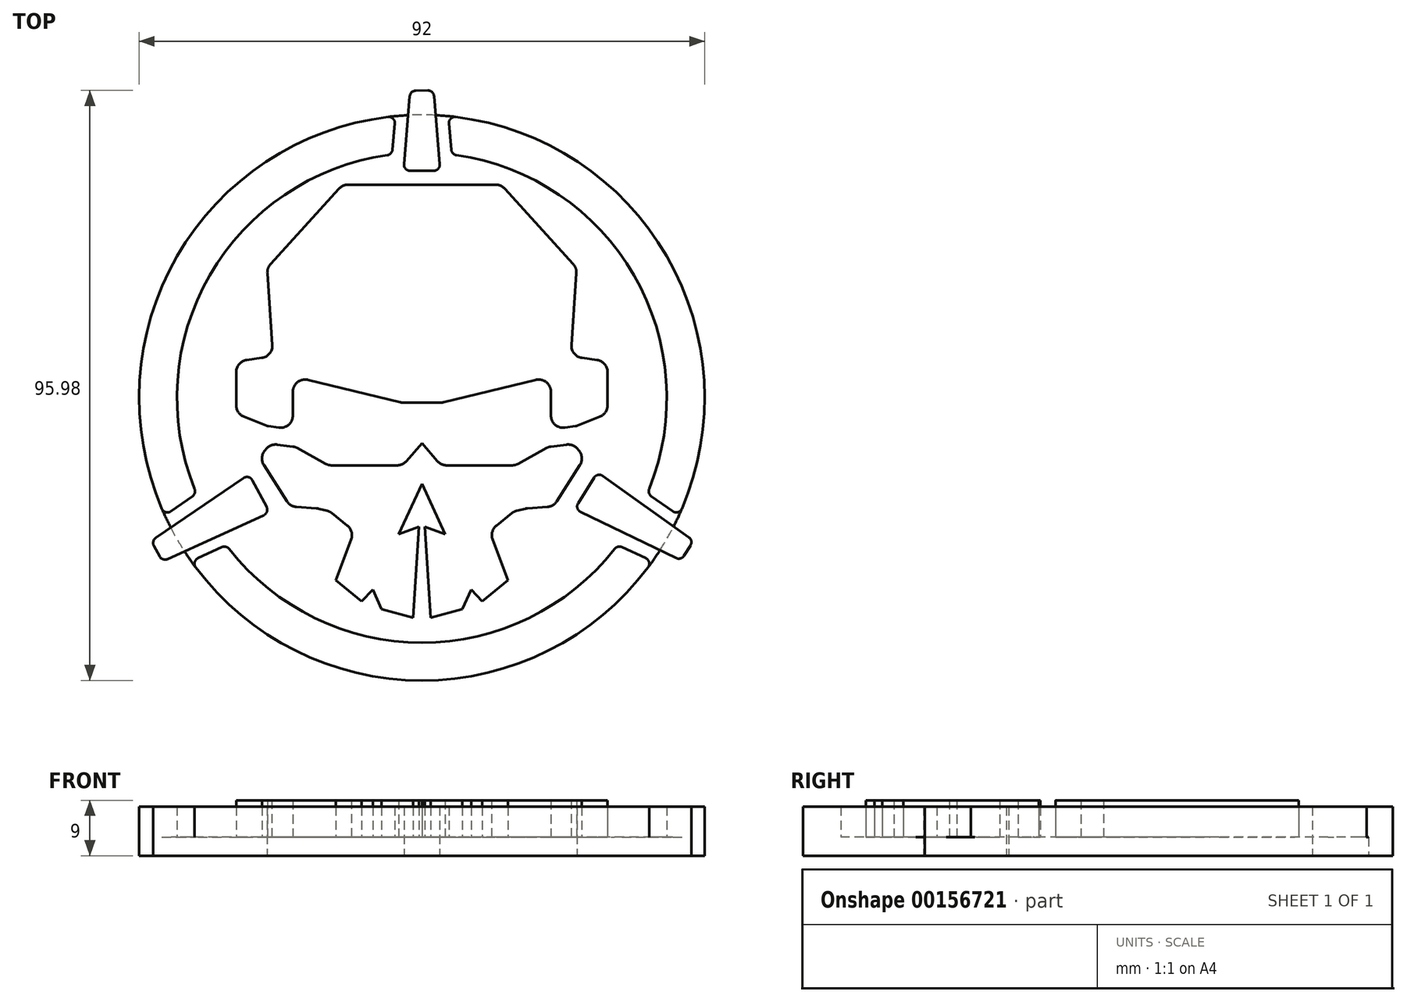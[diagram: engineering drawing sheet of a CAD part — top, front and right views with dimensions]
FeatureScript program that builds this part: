
annotation { "Feature Type Name" : "Feature", "Feature Type Description" : "" }
export const myFeature = defineFeature(function(context is Context, id is Id, definition is map)
    precondition{}
    {
        {
            var Q0;
            Q0=qCreatedBy(makeId("Top.planeOp"),FACE);
            cPlane(context, id + "F0", {"entities" : qUnion([Q0]), "cplaneType" : CPlaneType.OFFSET, "offset" : 3 * mm, "oppositeDirection" : true, "width" : 150 * mm, "height" : 150 * mm});
        }
        {
            var Q0;
            Q0=qCreatedBy(id+"F0.planeOp",FACE);
            var sketch = newSketch(context, id + "F1", { "sketchPlane" : qUnion([Q0])});
            skCircle(sketch, "E0", {"center": v(0, 0) * mm, "radius": 46 * mm});
            skSolve(sketch);
        }
        {
            var Q0;
            Q0 = qSketchRegion(id + "F1", true);
            extrude(context, id + "F2", {"entities" : qUnion([Q0]), "depth" : 8 * mm});
        }
        {
            var Q0;
            Q0=qCreatedBy(makeId("Top.planeOp"),FACE);
            var sketch = newSketch(context, id + "F3", { "sketchPlane" : qUnion([Q0])});
            skCircle(sketch, "E1", {"center": v(0, 0) * mm, "radius": 39.85 * mm});
            skSolve(sketch);
        }
        {
            var Q0;
            Q0 = qSketchRegion(id + "F3", true);
            extrude(context, id + "F4", {"entities" : qUnion([Q0]), "depth" : 6 * mm});
        }
        {
            var Q0;
            Q0=makeQuery(id+"F4.opExtrude","SWEPT_BODY",BODY,{"disambiguationData":[OSD([sQuery(id+"F3.wireOp",EDGE,"E1")])]});
            var Q1;
            Q1=makeQuery(id+"F2.opExtrude","SWEPT_BODY",BODY,{"disambiguationData":[OSD([sQuery(id+"F1.wireOp",EDGE,"E0")])]});
            booleanBodies(context, id + "F5", {"operationType" : BooleanOperationType.SUBTRACTION, "tools" : qUnion([Q0]), "targets" : qUnion([Q1])});
        }
        {
            var Q0;
            Q0=qCreatedBy(makeId("Top.planeOp"),FACE);
            var sketch = newSketch(context, id + "F6", { "sketchPlane" : qUnion([Q0])});
            skLineSegment(sketch, "E2", {"start": v(-4.2, 46.75) * mm, "end": v(-5, 38) * mm});
            skLineSegment(sketch, "E3", {"start": v(-5, 38) * mm, "end": v(5, 38) * mm});
            skLineSegment(sketch, "E4", {"start": v(5, 38) * mm, "end": v(4.2, 46.75) * mm});
            skLineSegment(sketch, "E5", {"start": v(4.2, 46.75) * mm, "end": v(-4.2, 46.75) * mm});
            skSolve(sketch);
        }
        {
            var Q0;
            Q0 = qSketchRegion(id + "F6", true);
            extrude(context, id + "F7", {"entities" : qUnion([Q0]), "depth" : 25 * mm});
        }
        {
            var Q0;
            Q0=qCreatedBy(makeId("Right.planeOp"),FACE);
            var sketch = newSketch(context, id + "F8", { "sketchPlane" : qUnion([Q0])});
            skLineSegment(sketch, "E6", {"start": v(0, 40.83) * mm, "end": v(0, -33.75) * mm});
            skSolve(sketch);
        }
        {
            var Q0;
            Q0=makeQuery(id+"F7.opExtrude","SWEPT_BODY",BODY,{"disambiguationData":[OSD([sQuery(id+"F6.wireOp",EDGE,"E2"),sQuery(id+"F6.wireOp",EDGE,"E3"),sQuery(id+"F6.wireOp",EDGE,"E4"),sQuery(id+"F6.wireOp",EDGE,"E5")])]});
            var Q1;
            Q1=qCreatedBy(makeId("Origin.pointOp"),VERTEX);
            var Q2;
            Q2=sQuery(id+"F8.wireOp",EDGE,"E6");
            transform(context, id + "F9", {"entities" : qUnion([Q0]), "transformType" : TransformType.ROTATION, "transformAxis" : qUnion([Q2]), "angle" : 120 * degree, "makeCopy" : true});
        }
        {
            var Q0;
            Q0=makeQuery(id+"F9.opPattern","COPY",BODY,{"derivedFrom":makeQuery(id+"F7.opExtrude","SWEPT_BODY",BODY,{"disambiguationData":[OSD([sQuery(id+"F6.wireOp",EDGE,"E2"),sQuery(id+"F6.wireOp",EDGE,"E3"),sQuery(id+"F6.wireOp",EDGE,"E4"),sQuery(id+"F6.wireOp",EDGE,"E5")])]}),"instanceName":"1"});
            var Q1;
            Q1=sQuery(id+"F8.wireOp",EDGE,"E6");
            transform(context, id + "F10", {"entities" : qUnion([Q0]), "transformType" : TransformType.ROTATION, "transformAxis" : qUnion([Q1]), "angle" : 120 * degree, "makeCopy" : true});
        }
        {
            var Q0;
            Q0=makeQuery(id+"F10.opPattern","COPY",BODY,{"derivedFrom":makeQuery(id+"F9.opPattern","COPY",BODY,{"derivedFrom":makeQuery(id+"F7.opExtrude","SWEPT_BODY",BODY,{"disambiguationData":[OSD([sQuery(id+"F6.wireOp",EDGE,"E2"),sQuery(id+"F6.wireOp",EDGE,"E3"),sQuery(id+"F6.wireOp",EDGE,"E4"),sQuery(id+"F6.wireOp",EDGE,"E5")])]}),"instanceName":"1"}),"instanceName":"1"});
            var Q1;
            Q1=makeQuery(id+"F9.opPattern","COPY",BODY,{"derivedFrom":makeQuery(id+"F7.opExtrude","SWEPT_BODY",BODY,{"disambiguationData":[OSD([sQuery(id+"F6.wireOp",EDGE,"E2"),sQuery(id+"F6.wireOp",EDGE,"E3"),sQuery(id+"F6.wireOp",EDGE,"E4"),sQuery(id+"F6.wireOp",EDGE,"E5")])]}),"instanceName":"1"});
            var Q2;
            Q2=makeQuery(id+"F7.opExtrude","SWEPT_BODY",BODY,{"disambiguationData":[OSD([sQuery(id+"F6.wireOp",EDGE,"E2"),sQuery(id+"F6.wireOp",EDGE,"E3"),sQuery(id+"F6.wireOp",EDGE,"E4"),sQuery(id+"F6.wireOp",EDGE,"E5")])]});
            var Q3;
            Q3=makeQuery(id+"F2.opExtrude","SWEPT_BODY",BODY,{"disambiguationData":[OSD([sQuery(id+"F1.wireOp",EDGE,"E0")])]});
            booleanBodies(context, id + "F11", {"operationType" : BooleanOperationType.SUBTRACTION, "tools" : qUnion([Q0, Q1, Q2]), "targets" : qUnion([Q3])});
        }
        {
            var Q0;
            Q0=qCreatedBy(id+"F0.planeOp",FACE);
            var sketch = newSketch(context, id + "F12", { "sketchPlane" : qUnion([Q0])});
            skLineSegment(sketch, "E7", {"start": v(-1.9, 49.93) * mm, "end": v(-3, 36.9) * mm});
            skLineSegment(sketch, "E8", {"start": v(-3, 36.9) * mm, "end": v(3, 36.9) * mm});
            skLineSegment(sketch, "E9", {"start": v(3, 36.9) * mm, "end": v(1.9, 50) * mm});
            skLineSegment(sketch, "E10", {"start": v(1.9, 50) * mm, "end": v(-1.9, 49.93) * mm});
            skSolve(sketch);
        }
        {
            var Q0;
            Q0 = qSketchRegion(id + "F12", true);
            extrude(context, id + "F13", {"entities" : qUnion([Q0]), "depth" : 8 * mm});
        }
        {
            var Q0;
            Q0=qCreatedBy(id+"F0.planeOp",FACE);
            var sketch = newSketch(context, id + "F14", { "sketchPlane" : qUnion([Q0])});
            skLineSegment(sketch, "E11", {"start": v(44.18, -23.23) * mm, "end": v(28.57, -12.11) * mm});
            skLineSegment(sketch, "E12", {"start": v(28.57, -12.11) * mm, "end": v(24.82, -18.1) * mm});
            skLineSegment(sketch, "E13", {"start": v(24.82, -18.1) * mm, "end": v(42.18, -26.48) * mm});
            skLineSegment(sketch, "E14", {"start": v(42.18, -26.48) * mm, "end": v(44.18, -23.23) * mm});
            skSolve(sketch);
        }
        {
            var Q0;
            Q0 = qSketchRegion(id + "F14", true);
            extrude(context, id + "F15", {"entities" : qUnion([Q0]), "depth" : 8 * mm});
        }
        {
            var Q0;
            Q0=makeQuery(id+"F15.opExtrude","SWEPT_BODY",BODY,{"disambiguationData":[OSD([sQuery(id+"F14.wireOp",EDGE,"E11"),sQuery(id+"F14.wireOp",EDGE,"E12"),sQuery(id+"F14.wireOp",EDGE,"E13"),sQuery(id+"F14.wireOp",EDGE,"E14")])]});
            var Q1;
            Q1=sQuery(id+"F8.wireOp",EDGE,"E6");
            transform(context, id + "F16", {"entities" : qUnion([Q0]), "transformType" : TransformType.ROTATION, "transformAxis" : qUnion([Q1]), "angle" : 120 * degree, "makeCopy" : true});
        }
        {
            var Q0;
            Q0=qCreatedBy(makeId("Top.planeOp"),FACE);
            var sketch = newSketch(context, id + "F17", { "sketchPlane" : qUnion([Q0])});
            skLineSegment(sketch, "E15", {"start": v(12.9, 34.65) * mm, "end": v(-12.9, 34.65) * mm});
            skLineSegment(sketch, "E16", {"start": v(-12.9, 34.65) * mm, "end": v(-25.2, 21.1) * mm});
            skLineSegment(sketch, "E17", {"start": v(-25.2, 21.1) * mm, "end": v(-24.2, 6.73) * mm});
            skLineSegment(sketch, "E18", {"start": v(-24.2, 6.73) * mm, "end": v(-30.2, 5.9) * mm});
            skLineSegment(sketch, "E19", {"start": v(-30.2, 5.9) * mm, "end": v(-30.2, -2.6) * mm});
            skLineSegment(sketch, "E20", {"start": v(-30.2, -2.6) * mm, "end": v(-25.2, -4.6) * mm});
            skLineSegment(sketch, "E21", {"start": v(-25.2, -4.6) * mm, "end": v(-21, -5.2) * mm});
            skLineSegment(sketch, "E22", {"start": v(-21, -5.2) * mm, "end": v(-21, 3.5) * mm});
            skLineSegment(sketch, "E23", {"start": v(-21, 3.5) * mm, "end": v(-3.3, -0.8) * mm});
            skLineSegment(sketch, "E24", {"start": v(-3.3, -0.8) * mm, "end": v(3.3, -0.8) * mm});
            skLineSegment(sketch, "E25", {"start": v(3.3, -0.8) * mm, "end": v(21, 3.5) * mm});
            skLineSegment(sketch, "E26", {"start": v(21, 3.5) * mm, "end": v(21, -5.2) * mm});
            skLineSegment(sketch, "E27", {"start": v(21, -5.2) * mm, "end": v(25.2, -4.6) * mm});
            skLineSegment(sketch, "E28", {"start": v(25.2, -4.6) * mm, "end": v(30.2, -2.6) * mm});
            skLineSegment(sketch, "E29", {"start": v(30.2, -2.6) * mm, "end": v(30.2, 5.9) * mm});
            skLineSegment(sketch, "E30", {"start": v(30.2, 5.9) * mm, "end": v(24.2, 6.73) * mm});
            skLineSegment(sketch, "E31", {"start": v(24.2, 6.73) * mm, "end": v(25.2, 21.1) * mm});
            skLineSegment(sketch, "E32", {"start": v(25.2, 21.1) * mm, "end": v(12.9, 34.65) * mm});
            skSolve(sketch);
        }
        {
            var Q0;
            Q0 = qSketchRegion(id + "F17", true);
            extrude(context, id + "F18", {"entities" : qUnion([Q0]), "depth" : 6 * mm});
        }
        {
            var Q0;
            Q0=qCreatedBy(makeId("Top.planeOp"),FACE);
            var sketch = newSketch(context, id + "F19", { "sketchPlane" : qUnion([Q0])});
            skLineSegment(sketch, "E33", {"start": v(0, -7.4) * mm, "end": v(-3.1, -11) * mm});
            skLineSegment(sketch, "E34", {"start": v(-3.1, -11) * mm, "end": v(-15.2, -11) * mm});
            skLineSegment(sketch, "E35", {"start": v(-15.2, -11) * mm, "end": v(-20.6, -8) * mm});
            skLineSegment(sketch, "E36", {"start": v(-20.6, -8) * mm, "end": v(-24.6, -7.5) * mm});
            skLineSegment(sketch, "E37", {"start": v(-24.6, -7.5) * mm, "end": v(-26.5, -9.7) * mm});
            skLineSegment(sketch, "E38", {"start": v(-26.5, -9.7) * mm, "end": v(-21.4, -17.7) * mm});
            skLineSegment(sketch, "E39", {"start": v(-21.4, -17.7) * mm, "end": v(-17, -18) * mm});
            skLineSegment(sketch, "E40", {"start": v(-17, -18) * mm, "end": v(-15, -18.5) * mm});
            skLineSegment(sketch, "E41", {"start": v(-15, -18.5) * mm, "end": v(-11, -21.7) * mm});
            skLineSegment(sketch, "E42", {"start": v(-11, -21.7) * mm, "end": v(-14, -29.7) * mm});
            skLineSegment(sketch, "E43", {"start": v(-14, -29.7) * mm, "end": v(-9.8, -33.1) * mm});
            skLineSegment(sketch, "E44", {"start": v(-9.8, -33.1) * mm, "end": v(-8, -31.2) * mm});
            skLineSegment(sketch, "E45", {"start": v(-8, -31.2) * mm, "end": v(-6.6, -34.4) * mm});
            skLineSegment(sketch, "E46", {"start": v(-6.6, -34.4) * mm, "end": v(-1.4, -35.8) * mm});
            skLineSegment(sketch, "E47", {"start": v(-1.4, -35.8) * mm, "end": v(-0.5, -21) * mm});
            skLineSegment(sketch, "E48", {"start": v(-0.5, -21) * mm, "end": v(-3.8, -22.2) * mm});
            skLineSegment(sketch, "E49", {"start": v(-3.8, -22.2) * mm, "end": v(0, -14) * mm});
            skLineSegment(sketch, "E50", {"start": v(0, -14) * mm, "end": v(3.8, -22.2) * mm});
            skLineSegment(sketch, "E51", {"start": v(3.8, -22.2) * mm, "end": v(0.5, -21) * mm});
            skLineSegment(sketch, "E52", {"start": v(0.5, -21) * mm, "end": v(1.4, -35.8) * mm});
            skLineSegment(sketch, "E53", {"start": v(1.4, -35.8) * mm, "end": v(6.6, -34.4) * mm});
            skLineSegment(sketch, "E54", {"start": v(6.6, -34.4) * mm, "end": v(8, -31.2) * mm});
            skLineSegment(sketch, "E55", {"start": v(8, -31.2) * mm, "end": v(9.8, -33.1) * mm});
            skLineSegment(sketch, "E56", {"start": v(9.8, -33.1) * mm, "end": v(14, -29.7) * mm});
            skLineSegment(sketch, "E57", {"start": v(14, -29.7) * mm, "end": v(11, -21.7) * mm});
            skLineSegment(sketch, "E58", {"start": v(11, -21.7) * mm, "end": v(15, -18.5) * mm});
            skLineSegment(sketch, "E59", {"start": v(15, -18.5) * mm, "end": v(17, -18) * mm});
            skLineSegment(sketch, "E60", {"start": v(17, -18) * mm, "end": v(21.4, -17.7) * mm});
            skLineSegment(sketch, "E61", {"start": v(21.4, -17.7) * mm, "end": v(26.5, -9.7) * mm});
            skLineSegment(sketch, "E62", {"start": v(26.5, -9.7) * mm, "end": v(24.6, -7.5) * mm});
            skLineSegment(sketch, "E63", {"start": v(24.6, -7.5) * mm, "end": v(20.6, -8) * mm});
            skLineSegment(sketch, "E64", {"start": v(20.6, -8) * mm, "end": v(15.2, -11) * mm});
            skLineSegment(sketch, "E65", {"start": v(15.2, -11) * mm, "end": v(3.1, -11) * mm});
            skLineSegment(sketch, "E66", {"start": v(3.1, -11) * mm, "end": v(0, -7.4) * mm});
            skSolve(sketch);
        }
        {
            var Q0;
            Q0 = qSketchRegion(id + "F19", true);
            extrude(context, id + "F20", {"entities" : qUnion([Q0]), "depth" : 6 * mm});
        }
        {
            var Q0;
            Q0=makeQuery(id+"F13.opExtrude","SWEPT_EDGE",EDGE,{"disambiguationData":[OSD([sQuery(id+"F12.wireOp",EDGE,"E9"),sQuery(id+"F12.wireOp",EDGE,"E10")])]});
            var Q1;
            Q1=makeQuery(id+"F13.opExtrude","SWEPT_EDGE",EDGE,{"disambiguationData":[OSD([sQuery(id+"F12.wireOp",EDGE,"E7"),sQuery(id+"F12.wireOp",EDGE,"E10")])]});
            var Q2;
            Q2=makeQuery(id+"F13.opExtrude","SWEPT_EDGE",EDGE,{"disambiguationData":[OSD([sQuery(id+"F12.wireOp",EDGE,"E8"),sQuery(id+"F12.wireOp",EDGE,"E9")])]});
            var Q3;
            Q3=makeQuery(id+"F13.opExtrude","SWEPT_EDGE",EDGE,{"disambiguationData":[OSD([sQuery(id+"F12.wireOp",EDGE,"E7"),sQuery(id+"F12.wireOp",EDGE,"E8")])]});
            var Q4;
            Q4=makeQuery(id+"F16.opPattern","COPY",EDGE,{"derivedFrom":makeQuery(id+"F15.opExtrude","SWEPT_EDGE",EDGE,{"disambiguationData":[OSD([sQuery(id+"F14.wireOp",EDGE,"E12"),sQuery(id+"F14.wireOp",EDGE,"E13")])]}),"instanceName":"1"});
            var Q5;
            Q5=makeQuery(id+"F16.opPattern","COPY",EDGE,{"derivedFrom":makeQuery(id+"F15.opExtrude","SWEPT_EDGE",EDGE,{"disambiguationData":[OSD([sQuery(id+"F14.wireOp",EDGE,"E13"),sQuery(id+"F14.wireOp",EDGE,"E14")])]}),"instanceName":"1"});
            var Q6;
            Q6=makeQuery(id+"F16.opPattern","COPY",EDGE,{"derivedFrom":makeQuery(id+"F15.opExtrude","SWEPT_EDGE",EDGE,{"disambiguationData":[OSD([sQuery(id+"F14.wireOp",EDGE,"E11"),sQuery(id+"F14.wireOp",EDGE,"E14")])]}),"instanceName":"1"});
            var Q7;
            Q7=makeQuery(id+"F16.opPattern","COPY",EDGE,{"derivedFrom":makeQuery(id+"F15.opExtrude","SWEPT_EDGE",EDGE,{"disambiguationData":[OSD([sQuery(id+"F14.wireOp",EDGE,"E11"),sQuery(id+"F14.wireOp",EDGE,"E12")])]}),"instanceName":"1"});
            var Q8;
            Q8=makeQuery(id+"F15.opExtrude","SWEPT_EDGE",EDGE,{"disambiguationData":[OSD([sQuery(id+"F14.wireOp",EDGE,"E12"),sQuery(id+"F14.wireOp",EDGE,"E13")])]});
            var Q9;
            Q9=makeQuery(id+"F15.opExtrude","SWEPT_EDGE",EDGE,{"disambiguationData":[OSD([sQuery(id+"F14.wireOp",EDGE,"E11"),sQuery(id+"F14.wireOp",EDGE,"E12")])]});
            var Q10;
            Q10=makeQuery(id+"F15.opExtrude","SWEPT_EDGE",EDGE,{"disambiguationData":[OSD([sQuery(id+"F14.wireOp",EDGE,"E13"),sQuery(id+"F14.wireOp",EDGE,"E14")])]});
            var Q11;
            Q11=makeQuery(id+"F15.opExtrude","SWEPT_EDGE",EDGE,{"disambiguationData":[OSD([sQuery(id+"F14.wireOp",EDGE,"E11"),sQuery(id+"F14.wireOp",EDGE,"E14")])]});
            var Q12;
            Q12=makeQuery(id+"F11.opBoolean","INTERSECT",EDGE,{"derivedFrom":[makeQuery(id+"F2.opExtrude","SWEPT_FACE",FACE,{"disambiguationData":[OSD([sQuery(id+"F1.wireOp",EDGE,"E0")])]}),makeQuery(id+"F9.opPattern","COPY",FACE,{"derivedFrom":makeQuery(id+"F7.opExtrude","SWEPT_FACE",FACE,{"disambiguationData":[OSD([sQuery(id+"F6.wireOp",EDGE,"E4")])]}),"instanceName":"1"})]});
            var Q13;
            Q13=makeQuery(id+"F11.opBoolean","INTERSECT",EDGE,{"derivedFrom":[makeQuery(id+"F2.opExtrude","SWEPT_FACE",FACE,{"disambiguationData":[OSD([sQuery(id+"F1.wireOp",EDGE,"E0")])]}),makeQuery(id+"F9.opPattern","COPY",FACE,{"derivedFrom":makeQuery(id+"F7.opExtrude","SWEPT_FACE",FACE,{"disambiguationData":[OSD([sQuery(id+"F6.wireOp",EDGE,"E2")])]}),"instanceName":"1"})]});
            var Q14;
            Q14=makeQuery(id+"F11.opBoolean","INTERSECT",EDGE,{"derivedFrom":[makeQuery(id+"F5.opBoolean","COPY",FACE,{"derivedFrom":makeQuery(id+"F4.opExtrude","SWEPT_FACE",FACE,{"disambiguationData":[OSD([sQuery(id+"F3.wireOp",EDGE,"E1")])]})}),makeQuery(id+"F9.opPattern","COPY",FACE,{"derivedFrom":makeQuery(id+"F7.opExtrude","SWEPT_FACE",FACE,{"disambiguationData":[OSD([sQuery(id+"F6.wireOp",EDGE,"E2")])]}),"instanceName":"1"})]});
            var Q15;
            Q15=makeQuery(id+"F11.opBoolean","INTERSECT",EDGE,{"derivedFrom":[makeQuery(id+"F5.opBoolean","COPY",FACE,{"derivedFrom":makeQuery(id+"F4.opExtrude","SWEPT_FACE",FACE,{"disambiguationData":[OSD([sQuery(id+"F3.wireOp",EDGE,"E1")])]})}),makeQuery(id+"F9.opPattern","COPY",FACE,{"derivedFrom":makeQuery(id+"F7.opExtrude","SWEPT_FACE",FACE,{"disambiguationData":[OSD([sQuery(id+"F6.wireOp",EDGE,"E4")])]}),"instanceName":"1"})]});
            var Q16;
            Q16=makeQuery(id+"F11.opBoolean","INTERSECT",EDGE,{"derivedFrom":[makeQuery(id+"F2.opExtrude","SWEPT_FACE",FACE,{"disambiguationData":[OSD([sQuery(id+"F1.wireOp",EDGE,"E0")])]}),makeQuery(id+"F7.opExtrude","SWEPT_FACE",FACE,{"disambiguationData":[OSD([sQuery(id+"F6.wireOp",EDGE,"E4")])]})]});
            var Q17;
            Q17=makeQuery(id+"F11.opBoolean","INTERSECT",EDGE,{"derivedFrom":[makeQuery(id+"F2.opExtrude","SWEPT_FACE",FACE,{"disambiguationData":[OSD([sQuery(id+"F1.wireOp",EDGE,"E0")])]}),makeQuery(id+"F7.opExtrude","SWEPT_FACE",FACE,{"disambiguationData":[OSD([sQuery(id+"F6.wireOp",EDGE,"E2")])]})]});
            var Q18;
            Q18=makeQuery(id+"F11.opBoolean","INTERSECT",EDGE,{"derivedFrom":[makeQuery(id+"F5.opBoolean","COPY",FACE,{"derivedFrom":makeQuery(id+"F4.opExtrude","SWEPT_FACE",FACE,{"disambiguationData":[OSD([sQuery(id+"F3.wireOp",EDGE,"E1")])]})}),makeQuery(id+"F7.opExtrude","SWEPT_FACE",FACE,{"disambiguationData":[OSD([sQuery(id+"F6.wireOp",EDGE,"E2")])]})]});
            var Q19;
            Q19=makeQuery(id+"F11.opBoolean","INTERSECT",EDGE,{"derivedFrom":[makeQuery(id+"F5.opBoolean","COPY",FACE,{"derivedFrom":makeQuery(id+"F4.opExtrude","SWEPT_FACE",FACE,{"disambiguationData":[OSD([sQuery(id+"F3.wireOp",EDGE,"E1")])]})}),makeQuery(id+"F7.opExtrude","SWEPT_FACE",FACE,{"disambiguationData":[OSD([sQuery(id+"F6.wireOp",EDGE,"E4")])]})]});
            var Q20;
            Q20=makeQuery(id+"F11.opBoolean","INTERSECT",EDGE,{"derivedFrom":[makeQuery(id+"F2.opExtrude","SWEPT_FACE",FACE,{"disambiguationData":[OSD([sQuery(id+"F1.wireOp",EDGE,"E0")])]}),makeQuery(id+"F10.opPattern","COPY",FACE,{"derivedFrom":makeQuery(id+"F9.opPattern","COPY",FACE,{"derivedFrom":makeQuery(id+"F7.opExtrude","SWEPT_FACE",FACE,{"disambiguationData":[OSD([sQuery(id+"F6.wireOp",EDGE,"E4")])]}),"instanceName":"1"}),"instanceName":"1"})]});
            var Q21;
            Q21=makeQuery(id+"F11.opBoolean","INTERSECT",EDGE,{"derivedFrom":[makeQuery(id+"F2.opExtrude","SWEPT_FACE",FACE,{"disambiguationData":[OSD([sQuery(id+"F1.wireOp",EDGE,"E0")])]}),makeQuery(id+"F10.opPattern","COPY",FACE,{"derivedFrom":makeQuery(id+"F9.opPattern","COPY",FACE,{"derivedFrom":makeQuery(id+"F7.opExtrude","SWEPT_FACE",FACE,{"disambiguationData":[OSD([sQuery(id+"F6.wireOp",EDGE,"E2")])]}),"instanceName":"1"}),"instanceName":"1"})]});
            var Q22;
            Q22=makeQuery(id+"F11.opBoolean","INTERSECT",EDGE,{"derivedFrom":[makeQuery(id+"F5.opBoolean","COPY",FACE,{"derivedFrom":makeQuery(id+"F4.opExtrude","SWEPT_FACE",FACE,{"disambiguationData":[OSD([sQuery(id+"F3.wireOp",EDGE,"E1")])]})}),makeQuery(id+"F10.opPattern","COPY",FACE,{"derivedFrom":makeQuery(id+"F9.opPattern","COPY",FACE,{"derivedFrom":makeQuery(id+"F7.opExtrude","SWEPT_FACE",FACE,{"disambiguationData":[OSD([sQuery(id+"F6.wireOp",EDGE,"E4")])]}),"instanceName":"1"}),"instanceName":"1"})]});
            var Q23;
            Q23=makeQuery(id+"F11.opBoolean","INTERSECT",EDGE,{"derivedFrom":[makeQuery(id+"F5.opBoolean","COPY",FACE,{"derivedFrom":makeQuery(id+"F4.opExtrude","SWEPT_FACE",FACE,{"disambiguationData":[OSD([sQuery(id+"F3.wireOp",EDGE,"E1")])]})}),makeQuery(id+"F10.opPattern","COPY",FACE,{"derivedFrom":makeQuery(id+"F9.opPattern","COPY",FACE,{"derivedFrom":makeQuery(id+"F7.opExtrude","SWEPT_FACE",FACE,{"disambiguationData":[OSD([sQuery(id+"F6.wireOp",EDGE,"E2")])]}),"instanceName":"1"}),"instanceName":"1"})]});
            fillet(context, id + "F21", {"entities" : qUnion([Q0, Q1, Q2, Q3, Q4, Q5, Q6, Q7, Q8, Q9, Q10, Q11, Q12, Q13, Q14, Q15, Q16, Q17, Q18, Q19, Q20, Q21, Q22, Q23]), "radius" : 1 * mm, "tangentPropagation" : true, "allowEdgeOverflow" : false});
        }
        {
            var Q0;
            Q0=makeQuery(id+"F18.opExtrude","SWEPT_EDGE",EDGE,{"disambiguationData":[OSD([sQuery(id+"F17.wireOp",EDGE,"E29"),sQuery(id+"F17.wireOp",EDGE,"E30")])]});
            var Q1;
            Q1=makeQuery(id+"F18.opExtrude","SWEPT_EDGE",EDGE,{"disambiguationData":[OSD([sQuery(id+"F17.wireOp",EDGE,"E28"),sQuery(id+"F17.wireOp",EDGE,"E29")])]});
            var Q2;
            Q2=makeQuery(id+"F18.opExtrude","SWEPT_EDGE",EDGE,{"disambiguationData":[OSD([sQuery(id+"F17.wireOp",EDGE,"E30"),sQuery(id+"F17.wireOp",EDGE,"E31")])]});
            var Q3;
            Q3=makeQuery(id+"F18.opExtrude","SWEPT_EDGE",EDGE,{"disambiguationData":[OSD([sQuery(id+"F17.wireOp",EDGE,"E31"),sQuery(id+"F17.wireOp",EDGE,"E32")])]});
            var Q4;
            Q4=makeQuery(id+"F18.opExtrude","SWEPT_EDGE",EDGE,{"disambiguationData":[OSD([sQuery(id+"F17.wireOp",EDGE,"E15"),sQuery(id+"F17.wireOp",EDGE,"E32")])]});
            var Q5;
            Q5=makeQuery(id+"F18.opExtrude","SWEPT_EDGE",EDGE,{"disambiguationData":[OSD([sQuery(id+"F17.wireOp",EDGE,"E15"),sQuery(id+"F17.wireOp",EDGE,"E16")])]});
            var Q6;
            Q6=makeQuery(id+"F18.opExtrude","SWEPT_EDGE",EDGE,{"disambiguationData":[OSD([sQuery(id+"F17.wireOp",EDGE,"E16"),sQuery(id+"F17.wireOp",EDGE,"E17")])]});
            var Q7;
            Q7=makeQuery(id+"F18.opExtrude","SWEPT_EDGE",EDGE,{"disambiguationData":[OSD([sQuery(id+"F17.wireOp",EDGE,"E17"),sQuery(id+"F17.wireOp",EDGE,"E18")])]});
            var Q8;
            Q8=makeQuery(id+"F18.opExtrude","SWEPT_EDGE",EDGE,{"disambiguationData":[OSD([sQuery(id+"F17.wireOp",EDGE,"E18"),sQuery(id+"F17.wireOp",EDGE,"E19")])]});
            var Q9;
            Q9=makeQuery(id+"F18.opExtrude","SWEPT_EDGE",EDGE,{"disambiguationData":[OSD([sQuery(id+"F17.wireOp",EDGE,"E19"),sQuery(id+"F17.wireOp",EDGE,"E20")])]});
            var Q10;
            Q10=makeQuery(id+"F18.opExtrude","SWEPT_EDGE",EDGE,{"disambiguationData":[OSD([sQuery(id+"F17.wireOp",EDGE,"E20"),sQuery(id+"F17.wireOp",EDGE,"E21")])]});
            var Q11;
            Q11=makeQuery(id+"F18.opExtrude","SWEPT_EDGE",EDGE,{"disambiguationData":[OSD([sQuery(id+"F17.wireOp",EDGE,"E21"),sQuery(id+"F17.wireOp",EDGE,"E22")])]});
            var Q12;
            Q12=makeQuery(id+"F18.opExtrude","SWEPT_EDGE",EDGE,{"disambiguationData":[OSD([sQuery(id+"F17.wireOp",EDGE,"E22"),sQuery(id+"F17.wireOp",EDGE,"E23")])]});
            var Q13;
            Q13=makeQuery(id+"F18.opExtrude","SWEPT_EDGE",EDGE,{"disambiguationData":[OSD([sQuery(id+"F17.wireOp",EDGE,"E23"),sQuery(id+"F17.wireOp",EDGE,"E24")])]});
            var Q14;
            Q14=makeQuery(id+"F18.opExtrude","SWEPT_EDGE",EDGE,{"disambiguationData":[OSD([sQuery(id+"F17.wireOp",EDGE,"E24"),sQuery(id+"F17.wireOp",EDGE,"E25")])]});
            var Q15;
            Q15=makeQuery(id+"F18.opExtrude","SWEPT_EDGE",EDGE,{"disambiguationData":[OSD([sQuery(id+"F17.wireOp",EDGE,"E25"),sQuery(id+"F17.wireOp",EDGE,"E26")])]});
            var Q16;
            Q16=makeQuery(id+"F18.opExtrude","SWEPT_EDGE",EDGE,{"disambiguationData":[OSD([sQuery(id+"F17.wireOp",EDGE,"E26"),sQuery(id+"F17.wireOp",EDGE,"E27")])]});
            var Q17;
            Q17=makeQuery(id+"F18.opExtrude","SWEPT_EDGE",EDGE,{"disambiguationData":[OSD([sQuery(id+"F17.wireOp",EDGE,"E27"),sQuery(id+"F17.wireOp",EDGE,"E28")])]});
            fillet(context, id + "F22", {"entities" : qUnion([Q0, Q1, Q2, Q3, Q4, Q5, Q6, Q7, Q8, Q9, Q10, Q11, Q12, Q13, Q14, Q15, Q16, Q17]), "radius" : 2 * mm, "tangentPropagation" : true, "allowEdgeOverflow" : false});
        }
        {
            var Q0;
            Q0=makeQuery(id+"F20.opExtrude","SWEPT_EDGE",EDGE,{"disambiguationData":[OSD([sQuery(id+"F19.wireOp",EDGE,"E61"),sQuery(id+"F19.wireOp",EDGE,"E62")])]});
            var Q1;
            Q1=makeQuery(id+"F20.opExtrude","SWEPT_EDGE",EDGE,{"disambiguationData":[OSD([sQuery(id+"F19.wireOp",EDGE,"E60"),sQuery(id+"F19.wireOp",EDGE,"E61")])]});
            var Q2;
            Q2=makeQuery(id+"F20.opExtrude","SWEPT_EDGE",EDGE,{"disambiguationData":[OSD([sQuery(id+"F19.wireOp",EDGE,"E59"),sQuery(id+"F19.wireOp",EDGE,"E60")])]});
            var Q3;
            Q3=makeQuery(id+"F20.opExtrude","SWEPT_EDGE",EDGE,{"disambiguationData":[OSD([sQuery(id+"F19.wireOp",EDGE,"E58"),sQuery(id+"F19.wireOp",EDGE,"E59")])]});
            var Q4;
            Q4=makeQuery(id+"F20.opExtrude","SWEPT_EDGE",EDGE,{"disambiguationData":[OSD([sQuery(id+"F19.wireOp",EDGE,"E57"),sQuery(id+"F19.wireOp",EDGE,"E58")])]});
            var Q5;
            Q5=makeQuery(id+"F20.opExtrude","SWEPT_EDGE",EDGE,{"disambiguationData":[OSD([sQuery(id+"F19.wireOp",EDGE,"E41"),sQuery(id+"F19.wireOp",EDGE,"E42")])]});
            var Q6;
            Q6=makeQuery(id+"F20.opExtrude","SWEPT_EDGE",EDGE,{"disambiguationData":[OSD([sQuery(id+"F19.wireOp",EDGE,"E40"),sQuery(id+"F19.wireOp",EDGE,"E41")])]});
            var Q7;
            Q7=makeQuery(id+"F20.opExtrude","SWEPT_EDGE",EDGE,{"disambiguationData":[OSD([sQuery(id+"F19.wireOp",EDGE,"E39"),sQuery(id+"F19.wireOp",EDGE,"E40")])]});
            var Q8;
            Q8=makeQuery(id+"F20.opExtrude","SWEPT_EDGE",EDGE,{"disambiguationData":[OSD([sQuery(id+"F19.wireOp",EDGE,"E38"),sQuery(id+"F19.wireOp",EDGE,"E39")])]});
            var Q9;
            Q9=makeQuery(id+"F20.opExtrude","SWEPT_EDGE",EDGE,{"disambiguationData":[OSD([sQuery(id+"F19.wireOp",EDGE,"E37"),sQuery(id+"F19.wireOp",EDGE,"E38")])]});
            var Q10;
            Q10=makeQuery(id+"F20.opExtrude","SWEPT_EDGE",EDGE,{"disambiguationData":[OSD([sQuery(id+"F19.wireOp",EDGE,"E36"),sQuery(id+"F19.wireOp",EDGE,"E37")])]});
            var Q11;
            Q11=makeQuery(id+"F20.opExtrude","SWEPT_EDGE",EDGE,{"disambiguationData":[OSD([sQuery(id+"F19.wireOp",EDGE,"E35"),sQuery(id+"F19.wireOp",EDGE,"E36")])]});
            var Q12;
            Q12=makeQuery(id+"F20.opExtrude","SWEPT_EDGE",EDGE,{"disambiguationData":[OSD([sQuery(id+"F19.wireOp",EDGE,"E34"),sQuery(id+"F19.wireOp",EDGE,"E35")])]});
            var Q13;
            Q13=makeQuery(id+"F20.opExtrude","SWEPT_EDGE",EDGE,{"disambiguationData":[OSD([sQuery(id+"F19.wireOp",EDGE,"E33"),sQuery(id+"F19.wireOp",EDGE,"E34")])]});
            var Q14;
            Q14=makeQuery(id+"F20.opExtrude","SWEPT_EDGE",EDGE,{"disambiguationData":[OSD([sQuery(id+"F19.wireOp",EDGE,"E65"),sQuery(id+"F19.wireOp",EDGE,"E66")])]});
            var Q15;
            Q15=makeQuery(id+"F20.opExtrude","SWEPT_EDGE",EDGE,{"disambiguationData":[OSD([sQuery(id+"F19.wireOp",EDGE,"E64"),sQuery(id+"F19.wireOp",EDGE,"E65")])]});
            var Q16;
            Q16=makeQuery(id+"F20.opExtrude","SWEPT_EDGE",EDGE,{"disambiguationData":[OSD([sQuery(id+"F19.wireOp",EDGE,"E63"),sQuery(id+"F19.wireOp",EDGE,"E64")])]});
            var Q17;
            Q17=makeQuery(id+"F20.opExtrude","SWEPT_EDGE",EDGE,{"disambiguationData":[OSD([sQuery(id+"F19.wireOp",EDGE,"E62"),sQuery(id+"F19.wireOp",EDGE,"E63")])]});
            fillet(context, id + "F23", {"entities" : qUnion([Q0, Q1, Q2, Q3, Q4, Q5, Q6, Q7, Q8, Q9, Q10, Q11, Q12, Q13, Q14, Q15, Q16, Q17]), "radius" : 2 * mm, "tangentPropagation" : true, "allowEdgeOverflow" : false});
        }
        {
            var Q0;
            Q0=makeQuery(id+"F13.opExtrude","SWEPT_BODY",BODY,{"disambiguationData":[OSD([sQuery(id+"F12.wireOp",EDGE,"E7"),sQuery(id+"F12.wireOp",EDGE,"E8"),sQuery(id+"F12.wireOp",EDGE,"E9"),sQuery(id+"F12.wireOp",EDGE,"E10")])]});
            transform(context, id + "F24", {"entities" : qUnion([Q0]), "transformType" : TransformType.TRANSLATION_3D, "dx" : 0 * mm, "dy" : 0 * mm, "dz" : 0 * mm, "makeCopy" : true});
        }
        {
            var Q0;
            Q0=makeQuery(id+"F24.opPattern","COPY",BODY,{"derivedFrom":makeQuery(id+"F13.opExtrude","SWEPT_BODY",BODY,{"disambiguationData":[OSD([sQuery(id+"F12.wireOp",EDGE,"E7"),sQuery(id+"F12.wireOp",EDGE,"E8"),sQuery(id+"F12.wireOp",EDGE,"E9"),sQuery(id+"F12.wireOp",EDGE,"E10")])]}),"instanceName":"1"});
            deleteBodies(context, id + "F25", {"entities" : qUnion([Q0])});
        }
    });
